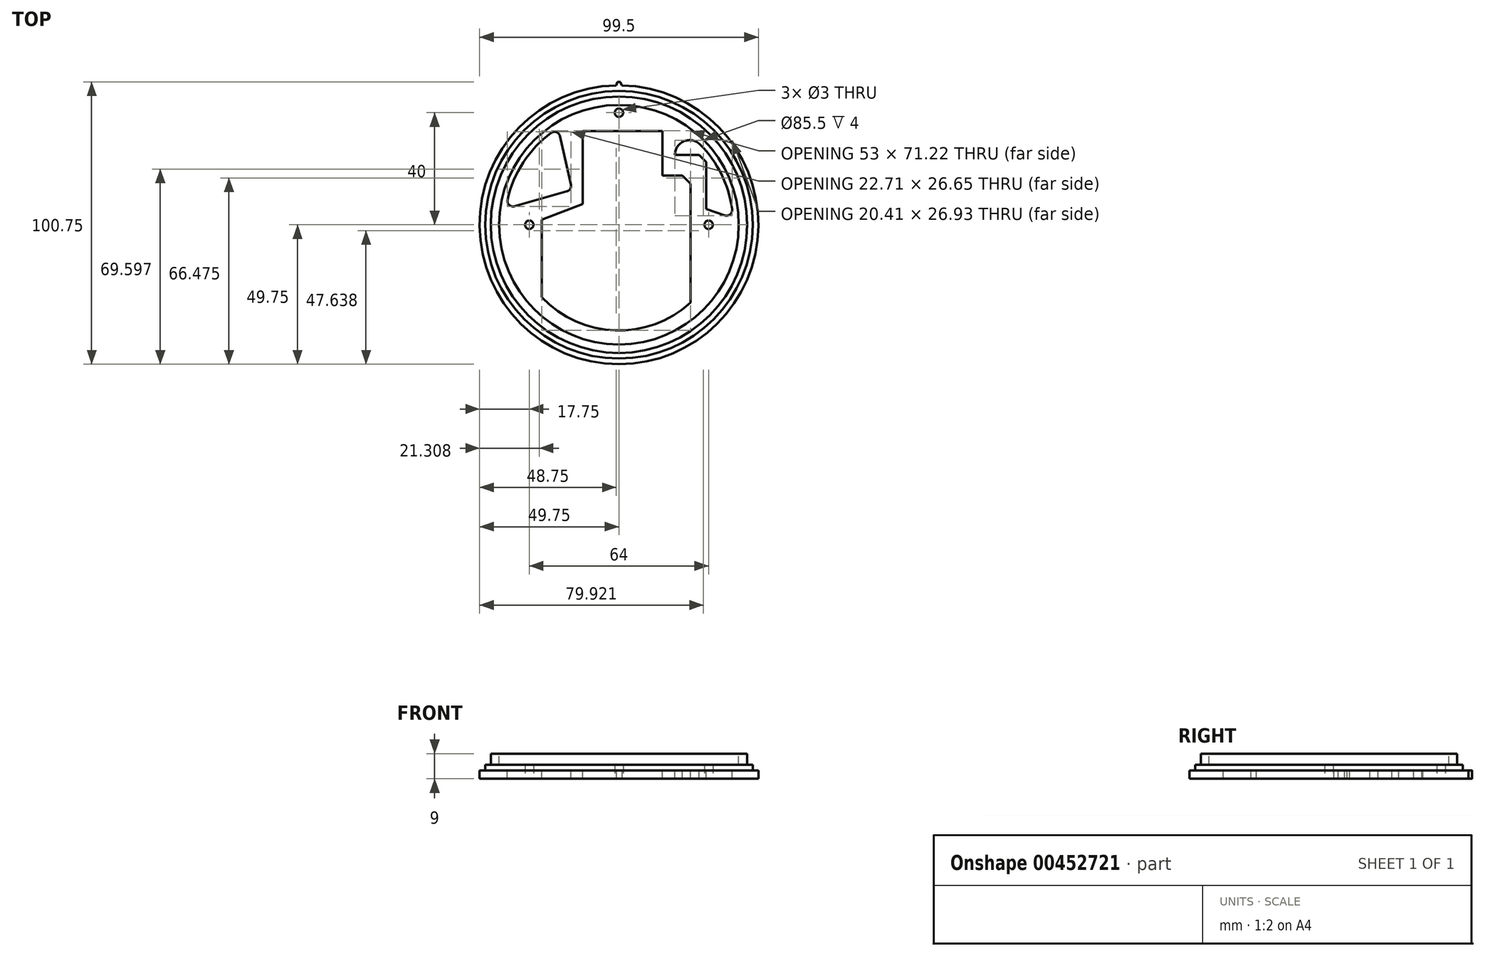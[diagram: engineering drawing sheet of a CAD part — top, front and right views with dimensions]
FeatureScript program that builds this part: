
annotation { "Feature Type Name" : "Feature", "Feature Type Description" : "" }
export const myFeature = defineFeature(function(context is Context, id is Id, definition is map)
    precondition{}
    {
        {
            var Q0;
            Q0=qCreatedBy(makeId("Top.planeOp"),FACE);
            var sketch = newSketch(context, id + "F0", { "sketchPlane" : qUnion([Q0])});
            skCircle(sketch, "E0", {"center": v(0, 0) * mm, "radius": 49.75 * mm, "construction": true});
            skCircle(sketch, "E1", {"center": v(0, 0) * mm, "radius": 51 * mm, "construction": true});
            skSolve(sketch);
        }
        {
            var Q0;
            Q0=qCreatedBy(makeId("Front.planeOp"),FACE);
            var sketch = newSketch(context, id + "F1", { "sketchPlane" : qUnion([Q0])});
            skLineSegment(sketch, "E2", {"start": v(0, 0) * mm, "end": v(49.75, 0) * mm});
            skLineSegment(sketch, "E3", {"start": v(49.75, 0) * mm, "end": v(49.75, 3) * mm});
            skLineSegment(sketch, "E4", {"start": v(49.75, 3) * mm, "end": v(47.75, 3) * mm});
            skLineSegment(sketch, "E5", {"start": v(47.75, 3) * mm, "end": v(47.75, 5) * mm});
            skLineSegment(sketch, "E6", {"start": v(47.75, 5) * mm, "end": v(45.75, 5) * mm});
            skLineSegment(sketch, "E7", {"start": v(45.75, 5) * mm, "end": v(45.75, 9) * mm});
            skLineSegment(sketch, "E8", {"start": v(45.75, 9) * mm, "end": v(42.75, 9) * mm});
            skLineSegment(sketch, "E9", {"start": v(42.75, 9) * mm, "end": v(42.75, 5) * mm});
            skLineSegment(sketch, "E10", {"start": v(42.75, 5) * mm, "end": v(0, 5) * mm});
            skLineSegment(sketch, "E11", {"start": v(0, 5) * mm, "end": v(0, 0) * mm});
            skSolve(sketch);
        }
        {
            var Q0;
            Q0 = qSketchRegion(id + "F1", true);
            var Q1;
            Q1=sQuery(id+"F1.wireOp",EDGE,"E11");
            revolve(context, id + "F2", {"entities" : qUnion([Q0]), "axis" : qUnion([Q1]), "revolveType" : RevolveType.FULL});
        }
        {
            var Q0;
            Q0=qCreatedBy(makeId("Top.planeOp"),FACE);
            var sketch = newSketch(context, id + "F3", { "sketchPlane" : qUnion([Q0])});
            skLineSegment(sketch, "E12", {"start": v(0, 0) * mm, "end": v(0, 51) * mm, "construction": true});
            skArc(sketch, "E13", {"start": v(0, 51) * mm, "mid": v(0.25, 51) * mm, "end": v(0.5, 51) * mm});
            skArc(sketch, "E14", {"start": v(0, 49.75) * mm, "mid": v(0.5, 49.75) * mm, "end": v(1, 49.74) * mm});
            skLineSegment(sketch, "E15", {"start": v(0.5, 51) * mm, "end": v(1, 49.74) * mm});
            skArc(sketch, "E16.MirrorCS", {"start": v(0, 51) * mm, "mid": v(-0.25, 51) * mm, "end": v(-0.5, 51) * mm});
            skLineSegment(sketch, "E17.MirrorCS", {"start": v(-0.5, 51) * mm, "end": v(-1, 49.74) * mm});
            skArc(sketch, "E18.MirrorCS", {"start": v(0, 49.75) * mm, "mid": v(-0.5, 49.75) * mm, "end": v(-1, 49.74) * mm});
            skSolve(sketch);
        }
        {
            var Q0;
            Q0 = qSketchRegion(id + "F3", true);
            var Q1;
            Q1=makeQuery(id+"F2.opRevolve","SWEPT_FACE",FACE,{"disambiguationData":[OSD([sQuery(id+"F1.wireOp",EDGE,"E4")])]});
            extrude(context, id + "F4", {"entities" : qUnion([Q0]), "operationType" : NewBodyOperationType.ADD, "endBound" : BoundingType.UP_TO_SURFACE, "endBoundEntityFace" : qUnion([Q1]), "depth" : 25 * mm});
        }
        {
            var Q0;
            Q0=makeQuery(id+"F4.opExtrude","SWEPT_EDGE",EDGE,{"disambiguationData":[OSD([sQuery(id+"F3.wireOp",EDGE,"E14"),sQuery(id+"F3.wireOp",EDGE,"E15")])]});
            var Q1;
            Q1=makeQuery(id+"F4.opExtrude","SWEPT_EDGE",EDGE,{"disambiguationData":[OSD([sQuery(id+"F3.wireOp",EDGE,"E13"),sQuery(id+"F3.wireOp",EDGE,"E15")])]});
            var Q2;
            Q2=makeQuery(id+"F4.opExtrude","SWEPT_EDGE",EDGE,{"disambiguationData":[OSD([sQuery(id+"F3.wireOp",EDGE,"E17.MirrorCS"),sQuery(id+"F3.wireOp",EDGE,"E18.MirrorCS")])]});
            var Q3;
            Q3=makeQuery(id+"F4.opExtrude","SWEPT_EDGE",EDGE,{"disambiguationData":[OSD([sQuery(id+"F3.wireOp",EDGE,"E16.MirrorCS"),sQuery(id+"F3.wireOp",EDGE,"E17.MirrorCS")])]});
            fillet(context, id + "F5", {"entities" : qUnion([Q0, Q1, Q2, Q3]), "radius" : 0.2 * mm, "tangentPropagation" : true, "allowEdgeOverflow" : false});
        }
        {
            var Q0;
            Q0=qCreatedBy(makeId("Top.planeOp"),FACE);
            var sketch = newSketch(context, id + "F6", { "sketchPlane" : qUnion([Q0])});
            skLineSegment(sketch, "E19", {"start": v(0, 0) * mm, "end": v(0, 40) * mm, "construction": true});
            skCircle(sketch, "E20", {"center": v(0, 40) * mm, "radius": 1.5 * mm});
            skCircle(sketch, "E21", {"center": v(32, 0) * mm, "radius": 1.5 * mm});
            skCircle(sketch, "E22.MirrorC", {"center": v(-32, 0) * mm, "radius": 1.5 * mm});
            skSolve(sketch);
        }
        {
            var Q0;
            Q0 = qSketchRegion(id + "F6", true);
            extrude(context, id + "F7", {"entities" : qUnion([Q0]), "operationType" : NewBodyOperationType.REMOVE, "endBound" : BoundingType.THROUGH_ALL, "depth" : 25 * mm});
        }
        {
            var Q0;
            Q0=makeQuery(id+"F2.opRevolve","SWEPT_FACE",FACE,{"disambiguationData":[OSD([sQuery(id+"F1.wireOp",EDGE,"E10")])]});
            var sketch = newSketch(context, id + "F8", { "sketchPlane" : qUnion([Q0])});
            skLineSegment(sketch, "E23", {"start": v(-12.95, 33.5) * mm, "end": v(15.47, 33.5) * mm});
            skLineSegment(sketch, "E24", {"start": v(15.47, 33.5) * mm, "end": v(15.47, 17.5) * mm});
            skLineSegment(sketch, "E25", {"start": v(15.47, 17.5) * mm, "end": v(22.66, 17.5) * mm});
            skLineSegment(sketch, "E26", {"start": v(22.66, 17.5) * mm, "end": v(25.5, 14.66) * mm});
            skLineSegment(sketch, "E27", {"start": v(25.5, 14.66) * mm, "end": v(25.5, -27.84) * mm});
            skArc(sketch, "E28.0", {"start": v(-27.5, -25.86) * mm, "mid": v(-1.4, -37.72) * mm, "end": v(25.5, -27.84) * mm});
            skLineSegment(sketch, "E29", {"start": v(-12.95, 33.5) * mm, "end": v(-12.95, 7.4) * mm});
            skLineSegment(sketch, "E30", {"start": v(-12.95, 7.4) * mm, "end": v(-27.5, 1.81) * mm});
            skLineSegment(sketch, "E31", {"start": v(-27.5, 1.81) * mm, "end": v(-27.5, -25.86) * mm});
            skArc(sketch, "E32.0", {"start": v(-24.2, 32.8) * mm, "mid": v(-34.12, 22.28) * mm, "end": v(-39.75, 8.96) * mm});
            skLineSegment(sketch, "E33", {"start": v(-37.25, 6.6) * mm, "end": v(-18.54, 11.94) * mm});
            skLineSegment(sketch, "E34", {"start": v(-17.13, 14.3) * mm, "end": v(-21.05, 31.63) * mm});
            skLineSegment(sketch, "E35", {"start": v(37.76, 3.36) * mm, "end": v(31.13, 5.58) * mm});
            skLineSegment(sketch, "E36", {"start": v(31.13, 5.58) * mm, "end": v(31.13, 22.44) * mm});
            skLineSegment(sketch, "E37", {"start": v(31.13, 22.44) * mm, "end": v(28.63, 24.94) * mm});
            skLineSegment(sketch, "E38", {"start": v(28.63, 24.94) * mm, "end": v(19.96, 24.94) * mm});
            skArc(sketch, "E39", {"start": v(19.96, 24.94) * mm, "mid": v(23.23, 29.82) * mm, "end": v(28.98, 28.65) * mm});
            skArc(sketch, "E40.0", {"start": v(40.37, 5.53) * mm, "mid": v(36.55, 18.01) * mm, "end": v(28.98, 28.65) * mm});
            skPoint(sketch, "E41.visualSharp", {"position": v(-16.72, 12.45) * mm});
            skArc(sketch, "E41.filletArc", {"start": v(-18.54, 11.94) * mm, "mid": v(-17.36, 12.84) * mm, "end": v(-17.13, 14.3) * mm});
            skPoint(sketch, "E42.visualSharp", {"position": v(-21.7, 34.5) * mm});
            skArc(sketch, "E42.filletArc", {"start": v(-21.05, 31.63) * mm, "mid": v(-22.3, 33.06) * mm, "end": v(-24.2, 32.8) * mm});
            skPoint(sketch, "E43.visualSharp", {"position": v(-40.35, 5.72) * mm});
            skArc(sketch, "E43.filletArc", {"start": v(-39.75, 8.96) * mm, "mid": v(-39.18, 7.07) * mm, "end": v(-37.25, 6.6) * mm});
            skPoint(sketch, "E44.visualSharp", {"position": v(40.68, 2.38) * mm});
            skArc(sketch, "E44.filletArc", {"start": v(37.76, 3.36) * mm, "mid": v(39.67, 3.71) * mm, "end": v(40.37, 5.53) * mm});
            skSolve(sketch);
        }
        {
            var Q0;
            Q0 = qSketchRegion(id + "F8", true);
            extrude(context, id + "F9", {"entities" : qUnion([Q0]), "operationType" : NewBodyOperationType.REMOVE, "endBound" : BoundingType.THROUGH_ALL, "oppositeDirection" : true, "depth" : 25 * mm});
        }
    });
